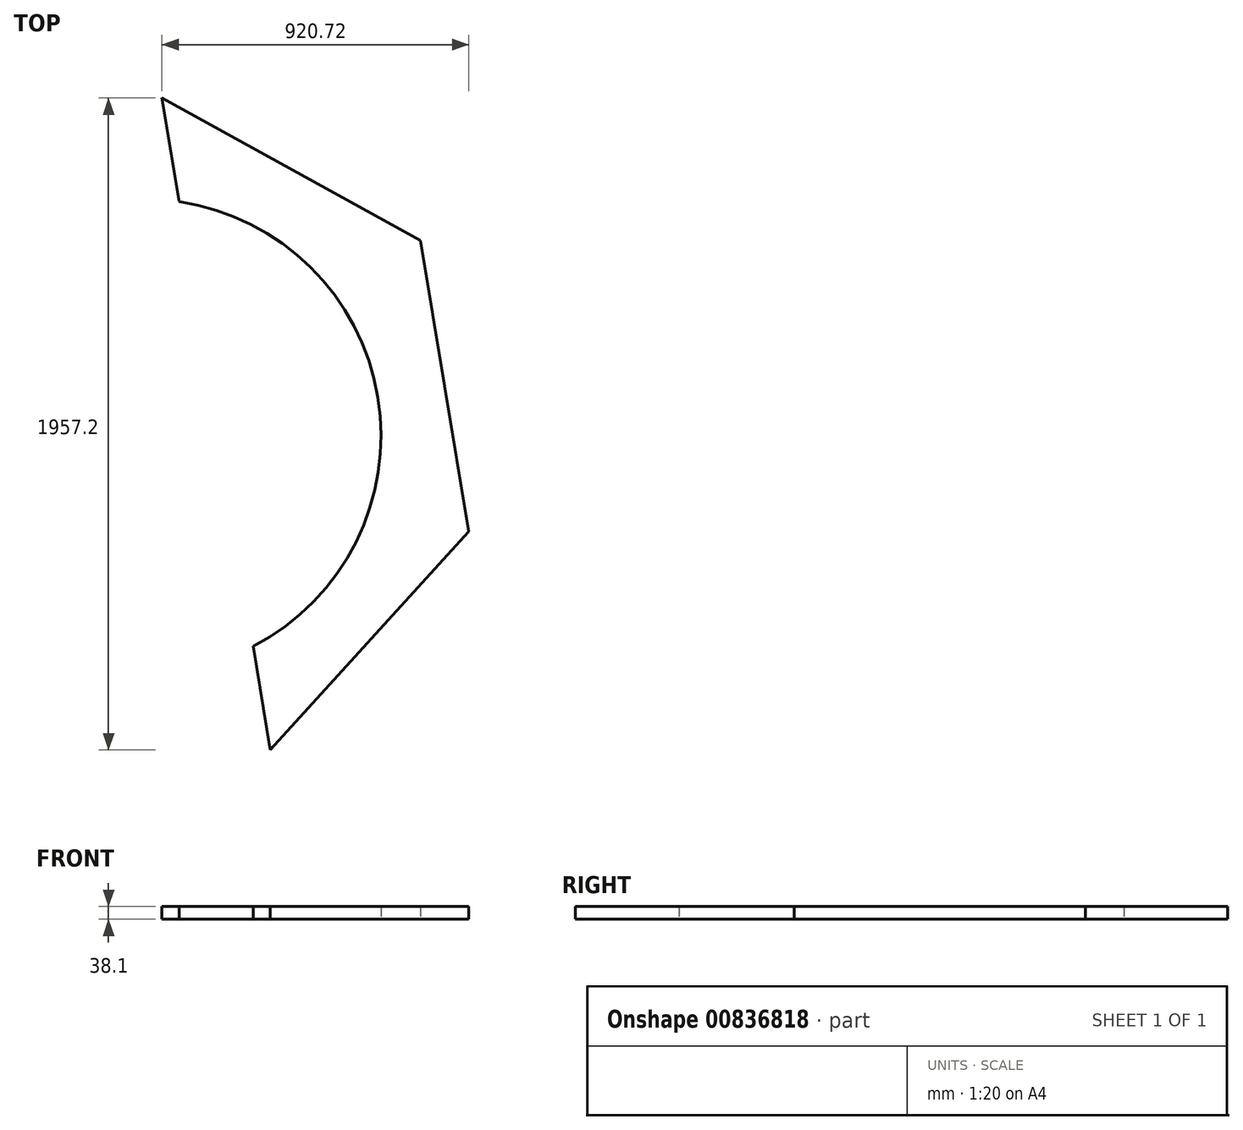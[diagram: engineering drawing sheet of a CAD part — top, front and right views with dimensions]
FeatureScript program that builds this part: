
annotation { "Feature Type Name" : "Feature", "Feature Type Description" : "" }
export const myFeature = defineFeature(function(context is Context, id is Id, definition is map)
    precondition{}
    {
        {
            var Q0;
            Q0=qCreatedBy(makeId("Top.planeOp"),FACE);
            var sketch = newSketch(context, id + "F0", { "sketchPlane" : qUnion([Q0])});
            skArc(sketch, "E0", {"start": v(327.36, -631.38) * mm, "mid": v(701.58, 116.56) * mm, "end": v(105.62, 703.31) * mm});
            skLineSegment(sketch, "E1.1", {"start": v(53.9, 1014.57) * mm, "end": v(829.45, 586.74) * mm});
            skLineSegment(sketch, "E1.2", {"start": v(829.45, 586.74) * mm, "end": v(974.62, -287.01) * mm});
            skLineSegment(sketch, "E1.3", {"start": v(974.62, -287.01) * mm, "end": v(379.07, -942.63) * mm});
            skPoint(sketch, "E1.0.midPoint", {"position": v(-402.73, 778.27) * mm});
            skLineSegment(sketch, "E2", {"start": v(53.9, 1014.57) * mm, "end": v(105.62, 703.31) * mm});
            skPoint(sketch, "E1.5.end.orphan", {"position": v(-859.37, 541.98) * mm});
            skPoint(sketch, "E1.4.end.orphan", {"position": v(-774.58, -657.48) * mm});
            skLineSegment(sketch, "E3.trimOffspring", {"start": v(327.36, -631.38) * mm, "end": v(379.07, -942.63) * mm});
            skPoint(sketch, "E4.start.orphan", {"position": v(-258.33, 703.31) * mm});
            skSolve(sketch);
        }
        {
            var Q0;
            Q0 = qSketchRegion(id + "F0", true);
            extrude(context, id + "F1", {"entities" : qUnion([Q0]), "depth" : 38.1 * mm, "offsetDistance" : 25.4 * mm});
        }
    });
